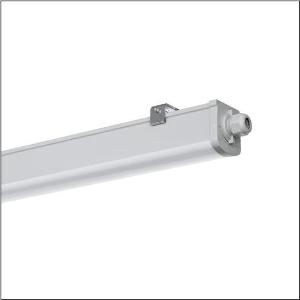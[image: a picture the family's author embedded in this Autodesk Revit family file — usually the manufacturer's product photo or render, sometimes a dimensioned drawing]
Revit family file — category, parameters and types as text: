
# Revit family: monsun_r__31_51fa207k450b_1d2e
name_source: partatom
category: Lighting Fixtures
units: mm (PartAtom-declared; Revit-internal decimal feet)

## family parameters
Cut with Voids When Loaded = No
Host = Face
Light Source = No
Part Type = Normal
Room Calculation Point = No
Round Connector Dimension = Use Diameter
Shared = No

## types (1)
- Monsun® 31 (1 x LED, 5100 lm, 38 W, 4000K)
    Apparent Load = 38 VA
    CIE Flux Codes = 42 72 91 92 100
    Color Rendering = 80
    Color Temperature = 4000K
    Default Elevation = 1800 mm
    Description = Monsun® 31, damp-proof luminaire, primary optical cover: diffuser, of PC, frosted, light emission: direct distribution, primary light characteristic: symmetric, installation type: surface-mounted, LED, rated luminous flux: 5.100lm, luminous efficacy: 134lm/W, light colour: 840, colour temperature: 4000K, control gear: ECG, with terminal, 3+1-pole, max. 2.5mm², through-wiring: 3x 2.5mm² + 1x 1.5mm², mains connection: 220..240V, AC, 50/60Hz, rated input power: 38W, housing, luminaire housing, of PC, light grey (RAL 7035), length: 1.158mm, width: 68mm, height: 76mm, protection rating (complete): IP66, insulation class (complete): insulation class II (safety insulation), certification: CE, ENEC, UKCA, protection symbol: D, impact resistance: IK08, permissible operating ambient temperature: -20..+40°C, corresponds to IFS (International Featured Standards) requirements for safety and quality in the food industry, contact your sales advisor before using the luminaires in applications with unclear chemical exposure, large temperature fluctuations or condensation-forming humidity, packaging unit: 1 piece
    Height = 77 mm
    Lamp = 1 x LED
    Lamp Light Flux = 5100 lm
    Lamp Power = 38 W
    Lamp count = 1
    Length = 1218 mm
    Luminous efficacy = 134 lm/W
    Manufacturer = Siteco
    ModVariant = No
    Model = 51FA207K450B
    Mounting Place = Ceiling
    Mounting Type = Surface mounted
    Number of Poles = 1
    OnlyDefault = Yes
    Power Factor = 1
    Product Name = Monsun® 31
    Product group = damp-proof luminaire
    ProductGroupID = 300
    Protection Class = Protection class II
    Protection Degree = IP 66
    RLX_Detail_Level = 1
    RLX_Emergency_Light_Flux = 0 lm
    RLX_Emergency_Type = 0
    RLX_Emergency_Type_DB = No
    RlxData = <blob elided: 32981 chars, md5=3533caa0>
    Socket = socket
    Standby Power = 0 W
    System Light Flux = 5100 lm
    System Power = 38 W
    Type Comments = Product without accessories
    Type Image = l_1006174.jpg
    URL = http://relux.com
    VarID = ---
    Voltage = 0 V
    Weight = 0.00 kg
    Width = 69 mm

## geometry (parser evidence)
native form markers: Blend x4, Sweep x11
no freeform markers — native parametric forms only
